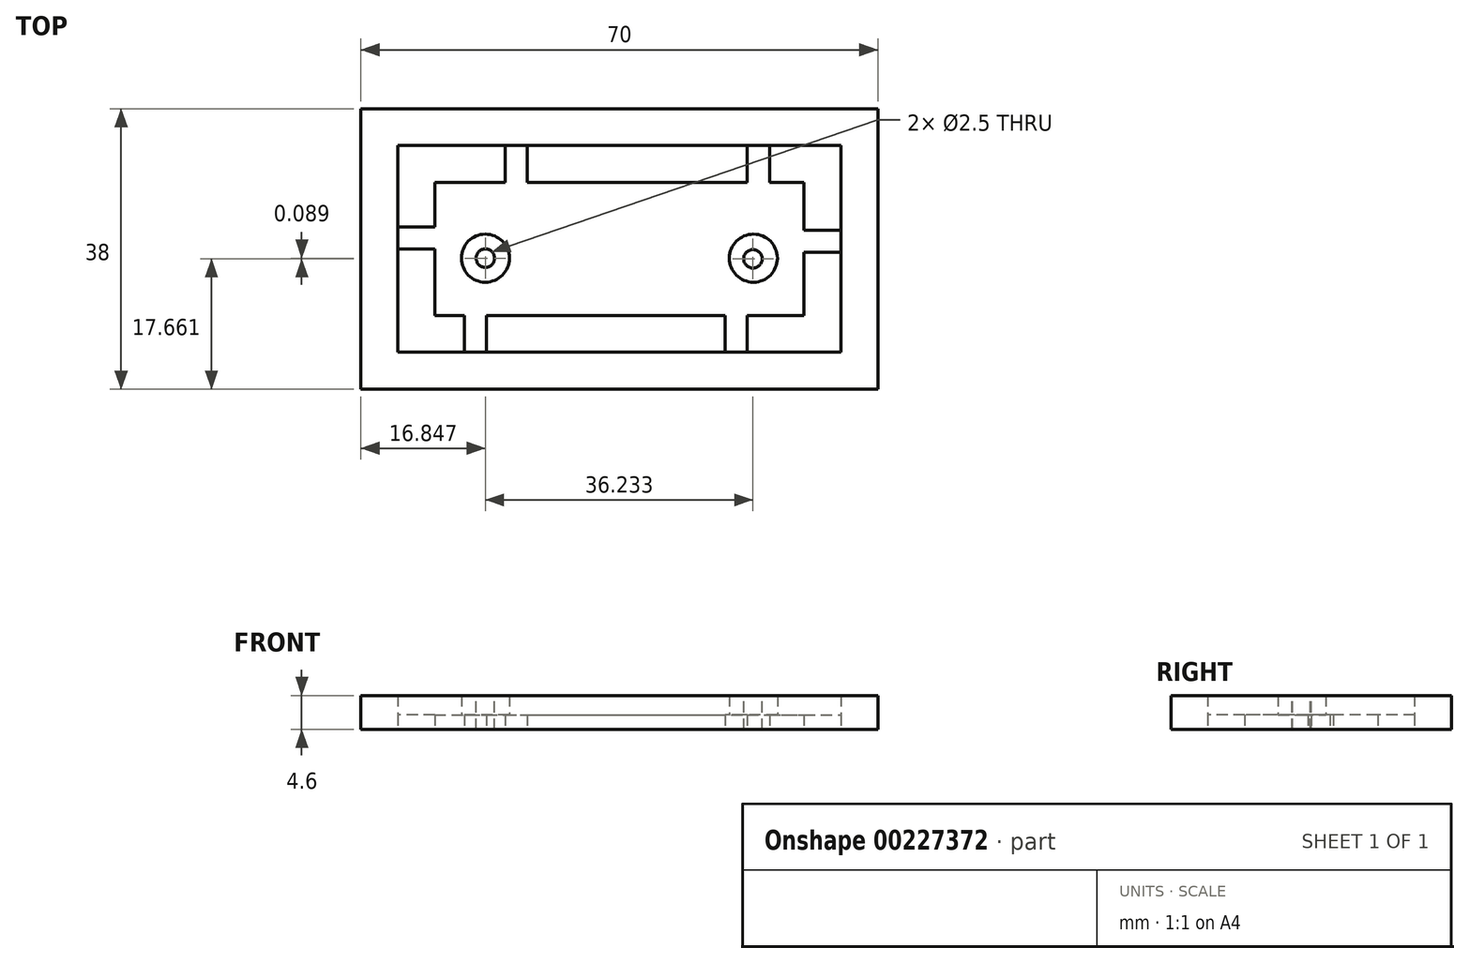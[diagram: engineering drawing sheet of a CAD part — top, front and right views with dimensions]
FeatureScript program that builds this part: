
annotation { "Feature Type Name" : "Feature", "Feature Type Description" : "" }
export const myFeature = defineFeature(function(context is Context, id is Id, definition is map)
    precondition{}
    {
        {
            var Q0;
            Q0=qCreatedBy(makeId("Top.planeOp"),FACE);
            var sketch = newSketch(context, id + "F0", { "sketchPlane" : qUnion([Q0])});
            skLineSegment(sketch, "E0.bottom", {"start": v(-23.15, 18) * mm, "end": v(26.85, 18) * mm});
            skLineSegment(sketch, "E0.top", {"start": v(-23.15, 0) * mm, "end": v(26.85, 0) * mm});
            skLineSegment(sketch, "E0.left", {"start": v(-23.15, 18) * mm, "end": v(-23.15, 0) * mm});
            skLineSegment(sketch, "E0.right", {"start": v(26.85, 18) * mm, "end": v(26.85, 0) * mm});
            skLineSegment(sketch, "E1.bottom", {"start": v(19.17, 23) * mm, "end": v(22.17, 23) * mm});
            skLineSegment(sketch, "E1.top", {"start": v(19.17, 18) * mm, "end": v(22.17, 18) * mm});
            skLineSegment(sketch, "E1.left", {"start": v(19.17, 23) * mm, "end": v(19.17, 18) * mm});
            skLineSegment(sketch, "E1.right", {"start": v(22.17, 23) * mm, "end": v(22.17, 18) * mm});
            skLineSegment(sketch, "E2.bottom", {"start": v(-19.17, 0) * mm, "end": v(-16.17, 0) * mm});
            skLineSegment(sketch, "E2.top", {"start": v(-19.17, -5) * mm, "end": v(-16.17, -5) * mm});
            skLineSegment(sketch, "E2.left", {"start": v(-19.17, 0) * mm, "end": v(-19.17, -5) * mm});
            skLineSegment(sketch, "E2.right", {"start": v(-16.17, 0) * mm, "end": v(-16.17, -5) * mm});
            skPoint(sketch, "E3.oppositeSnap0", {"position": v(-23.15, 9) * mm});
            skLineSegment(sketch, "E3.bottom", {"start": v(-23.15, 12) * mm, "end": v(-28.15, 12) * mm});
            skLineSegment(sketch, "E3.top", {"start": v(-23.15, 9) * mm, "end": v(-28.15, 9) * mm});
            skLineSegment(sketch, "E3.left", {"start": v(-23.15, 12) * mm, "end": v(-23.15, 9) * mm});
            skLineSegment(sketch, "E3.right", {"start": v(-28.15, 12) * mm, "end": v(-28.15, 9) * mm});
            skLineSegment(sketch, "E4.bottom", {"start": v(26.85, 11.57) * mm, "end": v(31.85, 11.57) * mm});
            skLineSegment(sketch, "E4.top", {"start": v(26.85, 8.57) * mm, "end": v(31.85, 8.57) * mm});
            skLineSegment(sketch, "E4.left", {"start": v(26.85, 11.57) * mm, "end": v(26.85, 8.57) * mm});
            skLineSegment(sketch, "E4.right", {"start": v(31.85, 11.57) * mm, "end": v(31.85, 8.57) * mm});
            skLineSegment(sketch, "E5.MirrorCS", {"start": v(23.15, 0) * mm, "end": v(-26.85, 0) * mm});
            skLineSegment(sketch, "E6.MirrorCS", {"start": v(16.17, 0) * mm, "end": v(16.17, -5) * mm});
            skLineSegment(sketch, "E7.MirrorCS", {"start": v(19.17, -5) * mm, "end": v(16.17, -5) * mm});
            skLineSegment(sketch, "E8.MirrorCS", {"start": v(19.17, 0) * mm, "end": v(19.17, -5) * mm});
            skLineSegment(sketch, "E9.bottom", {"start": v(-13.6, 23) * mm, "end": v(-10.6, 23) * mm});
            skLineSegment(sketch, "E9.top", {"start": v(-13.6, 18) * mm, "end": v(-10.6, 18) * mm});
            skLineSegment(sketch, "E9.left", {"start": v(-13.6, 23) * mm, "end": v(-13.6, 18) * mm});
            skLineSegment(sketch, "E9.right", {"start": v(-10.6, 23) * mm, "end": v(-10.6, 18) * mm});
            skSolve(sketch);
        }
        {
            var Q0;
            Q0=makeQuery(id+"F0.imprint","IMPRINT",FACE,{"disambiguationData":[TD([[makeQuery(id+"F0.imprint","IMPRINT",EDGE,{"derivedFrom":sQuery(id+"F0.wireOp",EDGE,"E0.bottom")}),-1.0]])]});
            extrude(context, id + "F1", {"entities" : qUnion([Q0]), "depth" : 2 * mm});
        }
        {
            var Q0;
            Q0=makeQuery(id+"F1.opExtrude","CAP_FACE",FACE,{"disambiguationData":[OSD([sQuery(id+"F0.wireOp",EDGE,"E0.bottom"),sQuery(id+"F0.wireOp",EDGE,"E0.top"),sQuery(id+"F0.wireOp",EDGE,"E0.left"),sQuery(id+"F0.wireOp",EDGE,"E0.right")])],"isStart":false});
            var sketch = newSketch(context, id + "F2", { "sketchPlane" : qUnion([Q0])});
            skCircle(sketch, "E10", {"center": v(20, 7.75) * mm, "radius": 3.25 * mm});
            skCircle(sketch, "E11", {"center": v(-16.3, 7.75) * mm, "radius": 3.25 * mm});
            skSolve(sketch);
        }
        {
            var Q0;
            Q0 = qSketchRegion(id + "F2", true);
            extrude(context, id + "F3", {"entities" : qUnion([Q0]), "operationType" : NewBodyOperationType.ADD, "depth" : 2.6 * mm});
        }
        {
            var Q0;
            Q0=makeQuery(id+"F3.opExtrude","CAP_FACE",FACE,{"disambiguationData":[OSD([sQuery(id+"F2.wireOp",EDGE,"E10")])],"isStart":false});
            var sketch = newSketch(context, id + "F4", { "sketchPlane" : qUnion([Q0])});
            skSolve(sketch);
        }
        {
            var Q0;
            Q0=makeQuery(id+"F0.imprint","IMPRINT",FACE,{"disambiguationData":[TD([[makeQuery(id+"F0.imprint","IMPRINT",EDGE,{"derivedFrom":sQuery(id+"F0.wireOp",EDGE,"E1.bottom")}),-1.0]])]});
            extrude(context, id + "F5", {"entities" : qUnion([Q0]), "operationType" : NewBodyOperationType.ADD, "depth" : 2 * mm});
        }
        {
            var Q0;
            Q0=makeQuery(id+"F3.opExtrude","CAP_FACE",FACE,{"disambiguationData":[OSD([sQuery(id+"F2.wireOp",EDGE,"E11")])],"isStart":false});
            var sketch = newSketch(context, id + "F6", { "sketchPlane" : qUnion([Q0])});
            skCircle(sketch, "E12", {"center": v(-16.3, 7.75) * mm, "radius": 1.25 * mm});
            skSolve(sketch);
        }
        {
            var Q0;
            Q0 = qSketchRegion(id + "F6", true);
            extrude(context, id + "F7", {"entities" : qUnion([Q0]), "operationType" : NewBodyOperationType.REMOVE, "oppositeDirection" : true, "depth" : 25 * mm});
        }
        {
            var Q0;
            Q0=makeQuery(id+"F4.imprint","IMPRINT",FACE,{"disambiguationData":[TD([[makeQuery(id+"F4.imprint","IMPRINT",EDGE,{"derivedFrom":makeQuery(id+"F3.opExtrude","CAP_EDGE",EDGE,{"disambiguationData":[OSD([sQuery(id+"F2.wireOp",EDGE,"E10")])],"isStart":false})}),1.0]])]});
            var sketch = newSketch(context, id + "F8", { "sketchPlane" : qUnion([Q0])});
            skCircle(sketch, "E13", {"center": v(19.93, 7.66) * mm, "radius": 1.25 * mm});
            skSolve(sketch);
        }
        {
            var Q0;
            Q0 = qSketchRegion(id + "F8", true);
            extrude(context, id + "F9", {"entities" : qUnion([Q0]), "operationType" : NewBodyOperationType.REMOVE, "oppositeDirection" : true, "depth" : 25 * mm});
        }
        {
            var Q0;
            Q0=makeQuery(id+"F0.imprint","IMPRINT",FACE,{"disambiguationData":[TD([[makeQuery(id+"F0.imprint","IMPRINT",EDGE,{"derivedFrom":sQuery(id+"F0.wireOp",EDGE,"E4.bottom")}),-1.0]])]});
            var Q1;
            Q1=makeQuery(id+"F0.imprint","IMPRINT",FACE,{"disambiguationData":[TD([[makeQuery(id+"F0.imprint","IMPRINT",EDGE,{"derivedFrom":sQuery(id+"F0.wireOp",EDGE,"E3.bottom")}),1.0]])]});
            extrude(context, id + "F10", {"entities" : qUnion([Q0, Q1]), "operationType" : NewBodyOperationType.ADD, "depth" : 2 * mm});
        }
        {
            var Q0;
            {var subQ0=sQuery(id+"F0.wireOp",EDGE,"9288da8d-5615-4d7a-8abe-8d1ef1cd2e1e0.MirrorCS");Q0=makeQuery(id+"F0.imprint","IMPRINT",FACE,{"disambiguationData":[TD([[makeQuery(id+"F0.imprint","IMPRINT",EDGE,{"derivedFrom":subQ0}),-1.0]])]});}
            var Q1;
            {var subQ0=sQuery(id+"F0.wireOp",EDGE,"E6.MirrorCS");Q1=makeQuery(id+"F0.imprint","IMPRINT",FACE,{"disambiguationData":[TD([[makeQuery(id+"F0.imprint","IMPRINT",EDGE,{"derivedFrom":subQ0}),1.0]])]});}
            extrude(context, id + "F11", {"entities" : qUnion([Q0, Q1]), "operationType" : NewBodyOperationType.ADD, "depth" : 2 * mm});
        }
        {
            var Q0;
            Q0=makeQuery(id+"F0.imprint","IMPRINT",FACE,{"disambiguationData":[TD([[makeQuery(id+"F0.imprint","IMPRINT",EDGE,{"derivedFrom":sQuery(id+"F0.wireOp",EDGE,"E2.top")}),1.0]])]});
            extrude(context, id + "F12", {"entities" : qUnion([Q0]), "operationType" : NewBodyOperationType.ADD, "depth" : 2 * mm});
        }
        {
            var Q0;
            Q0=makeQuery(id+"F0.imprint","IMPRINT",FACE,{"disambiguationData":[TD([[makeQuery(id+"F0.imprint","IMPRINT",EDGE,{"derivedFrom":sQuery(id+"F0.wireOp",EDGE,"E9.bottom")}),-1.0]])]});
            extrude(context, id + "F13", {"entities" : qUnion([Q0]), "operationType" : NewBodyOperationType.ADD, "depth" : 2 * mm});
        }
        {
            var Q0;
            Q0=qCreatedBy(makeId("Top.planeOp"),FACE);
            var sketch = newSketch(context, id + "F14", { "sketchPlane" : qUnion([Q0])});
            skLineSegment(sketch, "E14.bottom", {"start": v(-28.15, 23) * mm, "end": v(31.85, 23) * mm});
            skLineSegment(sketch, "E14.top", {"start": v(-28.15, -5) * mm, "end": v(31.85, -5) * mm});
            skLineSegment(sketch, "E14.left", {"start": v(-28.15, 23) * mm, "end": v(-28.15, -5) * mm});
            skLineSegment(sketch, "E14.right", {"start": v(31.85, 23) * mm, "end": v(31.85, -5) * mm});
            skLineSegment(sketch, "E15.bottom", {"start": v(-33.15, 28) * mm, "end": v(36.85, 28) * mm});
            skLineSegment(sketch, "E15.top", {"start": v(-33.15, -10) * mm, "end": v(36.85, -10) * mm});
            skLineSegment(sketch, "E15.left", {"start": v(-33.15, 28) * mm, "end": v(-33.15, -10) * mm});
            skLineSegment(sketch, "E15.right", {"start": v(36.85, 28) * mm, "end": v(36.85, -10) * mm});
            skSolve(sketch);
        }
        {
            var Q0;
            Q0=makeQuery(id+"F14.imprint","IMPRINT",FACE,{"disambiguationData":[TD([[makeQuery(id+"F14.imprint","IMPRINT",EDGE,{"derivedFrom":sQuery(id+"F14.wireOp",EDGE,"E14.bottom")}),1.0]])]});
            extrude(context, id + "F15", {"entities" : qUnion([Q0]), "operationType" : NewBodyOperationType.ADD, "depth" : 4.6 * mm});
        }
    });
